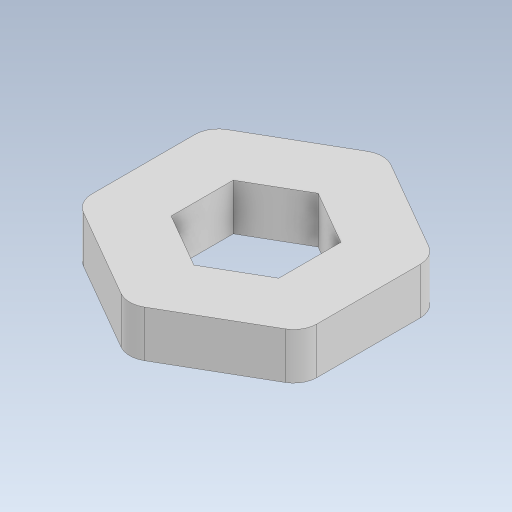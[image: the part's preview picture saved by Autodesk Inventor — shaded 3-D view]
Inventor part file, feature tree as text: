
AUTODESK INVENTOR PART (.ipt)
format: ipt  version: 2023 (Build 270158000, 158)  size: 292,352 bytes
history: native  units: in
note: dims shown in document units (in); Inventor stores cm internally (conversion verified against a paired STEP export)
features: extrude x1, fillet x1, sketch x1
ambient origin geometry x8: Origin, YZ Plane, XZ Plane, XY Plane, X Axis, Y Axis, Z Axis, Center Point
bodies: Solid1 (feature_tree)
feature tree (3):
  extrude  "Extrusion1"  Depth=0.7in
  fillet  "Fillet1"  Radius=0.25in
  sketch  "Sketch1"  dims[d0=0.3346in d1=0.7in d2=0.25in d3=0.0in d4=0.125in]
